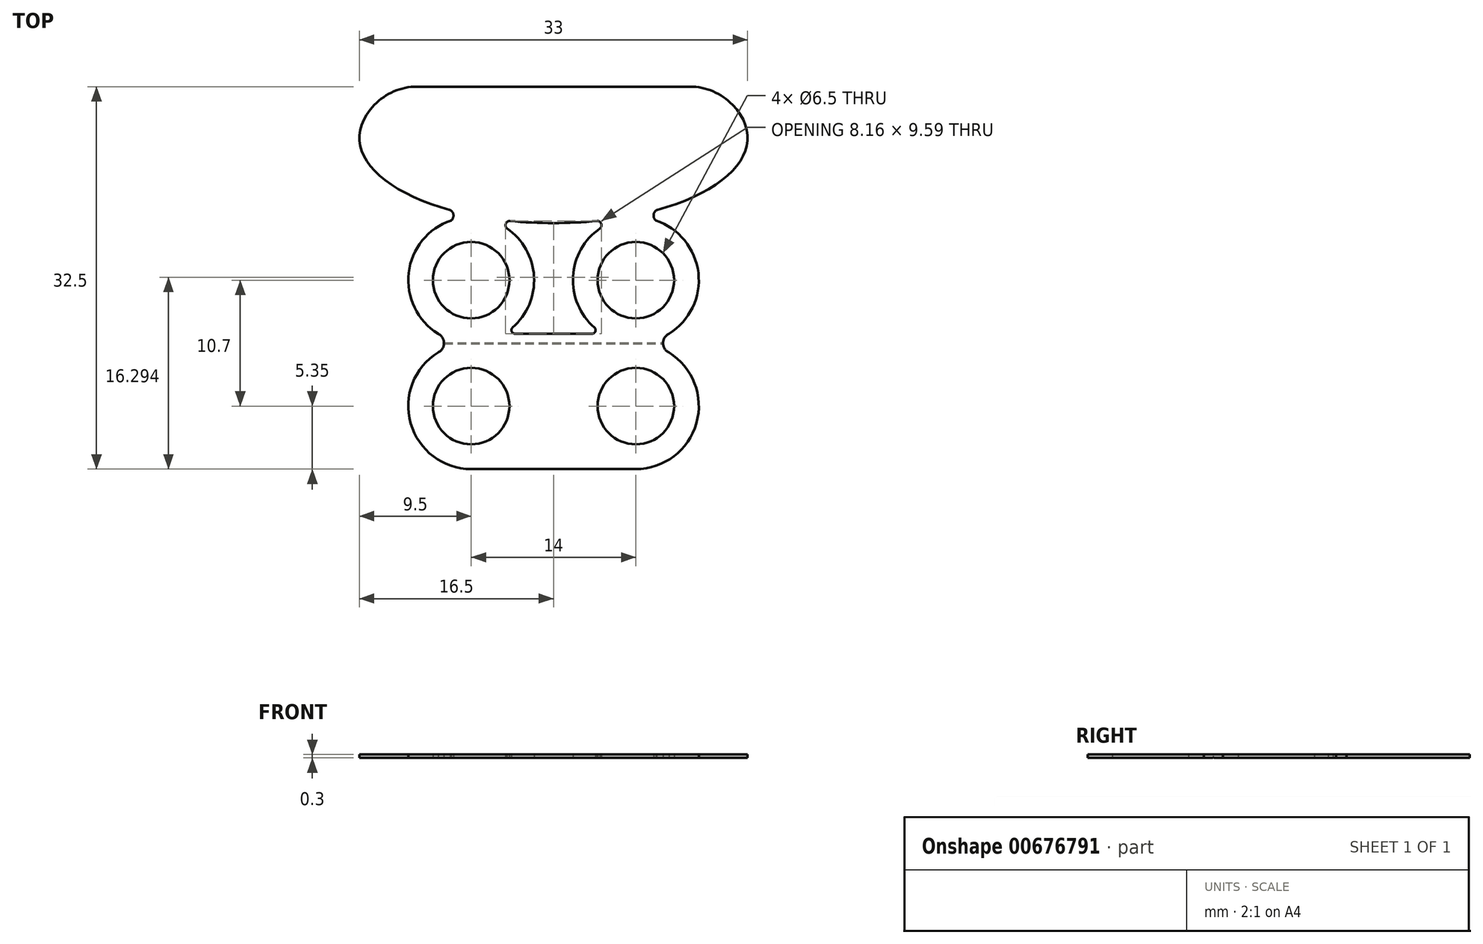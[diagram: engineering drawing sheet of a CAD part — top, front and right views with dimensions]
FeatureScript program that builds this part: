
annotation { "Feature Type Name" : "Feature", "Feature Type Description" : "" }
export const myFeature = defineFeature(function(context is Context, id is Id, definition is map)
    precondition{}
    {
        {
            var Q0;
            Q0=qCreatedBy(makeId("Top.planeOp"),FACE);
            var sketch = newSketch(context, id + "F0", { "sketchPlane" : qUnion([Q0])});
            skLineSegment(sketch, "E0", {"start": v(-13.2, 4.35) * mm, "end": v(13.2, 4.35) * mm});
            skPoint(sketch, "E1", {"position": v(0, -7.25) * mm});
            skCircle(sketch, "E2", {"center": v(-7, -12.1) * mm, "radius": 3.25 * mm});
            skLineSegment(sketch, "E3", {"start": v(0, 24.36) * mm, "end": v(0, -25.37) * mm, "construction": true});
            skPoint(sketch, "E4", {"position": v(-7, -17.45) * mm});
            skEllipticalArc(sketch, "E5", {});
            skEllipticalArc(sketch, "E6", {"construction": true});
            skEllipticalArc(sketch, "E7", {"construction": true});
            skEllipticalArc(sketch, "E8", {});
            skArc(sketch, "E9", {"start": v(-8.7, -7.03) * mm, "mid": v(-12.32, -11.56) * mm, "end": v(-9.68, -16.73) * mm});
            skArc(sketch, "E10", {"start": v(-3.96, -7.7) * mm, "mid": v(-6.25, -6.8) * mm, "end": v(-8.7, -7.03) * mm, "construction": true});
            skCircle(sketch, "E11.MirrorC", {"center": v(7, -12.1) * mm, "radius": 3.25 * mm});
            skArc(sketch, "E12.MirrorCS", {"start": v(8.7, -7.03) * mm, "mid": v(12.32, -11.56) * mm, "end": v(9.68, -16.73) * mm});
            skEllipticalArc(sketch, "E13", {"construction": true});
            skEllipticalArc(sketch, "E14", {});
            skLineSegment(sketch, "E15", {"start": v(-7, -17.45) * mm, "end": v(7, -17.45) * mm, "construction": true});
            skCircle(sketch, "E16.MirrorC", {"center": v(7, -22.8) * mm, "radius": 3.25 * mm});
            skCircle(sketch, "E17.MirrorC", {"center": v(-7, -22.8) * mm, "radius": 3.25 * mm});
            skPoint(sketch, "E18", {"position": v(-7, -28.15) * mm});
            skLineSegment(sketch, "E19", {"start": v(-7, -28.15) * mm, "end": v(7, -28.15) * mm});
            skLineSegment(sketch, "E20", {"start": v(-4.19, -16.65) * mm, "end": v(4.19, -16.65) * mm});
            skArc(sketch, "E21", {"start": v(-9.81, -18.25) * mm, "mid": v(-9.31, -17.45) * mm, "end": v(-9.81, -16.65) * mm});
            skLineSegment(sketch, "E22", {"start": v(-9.81, -16.65) * mm, "end": v(-9.81, -18.25) * mm, "construction": true});
            skArc(sketch, "E23.MirrorCS", {"start": v(9.81, -18.25) * mm, "mid": v(9.31, -17.45) * mm, "end": v(9.81, -16.65) * mm});
            skArc(sketch, "E24", {"start": v(-9.68, -16.73) * mm, "mid": v(-6.92, -17.45) * mm, "end": v(-4.19, -16.65) * mm, "construction": true});
            skArc(sketch, "E25", {"start": v(-4.19, -16.65) * mm, "mid": v(-1.65, -12.23) * mm, "end": v(-3.96, -7.7) * mm});
            skArc(sketch, "E26", {"start": v(-9.81, -18.25) * mm, "mid": v(-12.15, -24.26) * mm, "end": v(-7, -28.15) * mm});
            skArc(sketch, "E27", {"start": v(-7, -28.15) * mm, "mid": v(-1.85, -21.34) * mm, "end": v(-9.81, -18.25) * mm, "construction": true});
            skArc(sketch, "E28", {"start": v(9.68, -18.17) * mm, "mid": v(1.83, -21.41) * mm, "end": v(7, -28.15) * mm, "construction": true});
            skArc(sketch, "E29", {"start": v(7, -28.15) * mm, "mid": v(12.17, -24.19) * mm, "end": v(9.68, -18.17) * mm});
            skArc(sketch, "E30", {"start": v(9.68, -16.73) * mm, "mid": v(6.92, -17.45) * mm, "end": v(4.19, -16.65) * mm, "construction": true});
            skArc(sketch, "E31", {"start": v(4.19, -16.65) * mm, "mid": v(1.65, -12.23) * mm, "end": v(3.96, -7.7) * mm});
            skArc(sketch, "E32", {"start": v(-8.7, -7.03) * mm, "mid": v(-8.5, -6.57) * mm, "end": v(-8.77, -6.14) * mm});
            skArc(sketch, "E33", {"start": v(-3.73, -7.06) * mm, "mid": v(-4.06, -7.3) * mm, "end": v(-3.96, -7.7) * mm});
            skArc(sketch, "E34.MirrorCS", {"start": v(3.73, -7.06) * mm, "mid": v(4.06, -7.3) * mm, "end": v(3.96, -7.7) * mm});
            skArc(sketch, "E35.MirrorCS", {"start": v(8.7, -7.03) * mm, "mid": v(8.5, -6.57) * mm, "end": v(8.77, -6.14) * mm});
            const initialGuessF0  = {"E5": [0, 0, 1, 0, 0.0165, 0.00725, 2.49809154479651, 4.152051585814538], "E6": [0, 0, 1, 0, 0.0165, 0.00725, 0.6435011087932834, 2.49809154479651], "E7": [0, 0, 1, 0, 0.0165, 0.00725, 4.152051585814538, 4.484235995839755], "E8": [0, 0, 1, 0, 0.0165, 0.00725, 4.484235995839755, 4.940541964929625], "E13": [0, 0, 1, 0, 0.0165, 0.00725, 4.940541964929625, 5.272726374954841], "E14": [0, 0, 1, 0, 0.0165, 0.00725, 5.272726374954841, 0.6435011087932834]};
            skSetInitialGuess(sketch, initialGuessF0);
            skSolve(sketch);
        }
        {
            var Q0;
            Q0=makeQuery(id+"F0.imprint","IMPRINT",FACE,{"disambiguationData":[TD([[makeQuery(id+"F0.imprint","IMPRINT",EDGE,{"derivedFrom":sQuery(id+"F0.wireOp",EDGE,"E0")}),-1.0]])]});
            extrude(context, id + "F1", {"entities" : qUnion([Q0]), "depth" : 0.3 * mm, "offsetDistance" : 25 * mm});
        }
        {
            var Q0;
            Q0=makeQuery(id+"F1.opExtrude","SWEPT_EDGE",EDGE,{"disambiguationData":[OSD([sQuery(id+"F0.wireOp",EDGE,"E0"),sQuery(id+"F0.wireOp",EDGE,"E14")])]});
            var Q1;
            Q1=makeQuery(id+"F1.opExtrude","SWEPT_EDGE",EDGE,{"disambiguationData":[OSD([sQuery(id+"F0.wireOp",EDGE,"E0"),sQuery(id+"F0.wireOp",EDGE,"E5")])]});
            fillet(context, id + "F2", {"entities" : qUnion([Q0, Q1]), "radius" : 5 * mm, "tangentPropagation" : true, "allowEdgeOverflow" : false});
        }
        {
            var Q0;
            Q0=makeQuery(id+"F1.opExtrude","SWEPT_EDGE",EDGE,{"disambiguationData":[OSD([sQuery(id+"F0.wireOp",EDGE,"E20"),sQuery(id+"F0.wireOp",EDGE,"E25")])]});
            var Q1;
            Q1=makeQuery(id+"F1.opExtrude","SWEPT_EDGE",EDGE,{"disambiguationData":[OSD([sQuery(id+"F0.wireOp",EDGE,"E20"),sQuery(id+"F0.wireOp",EDGE,"E31")])]});
            fillet(context, id + "F3", {"entities" : qUnion([Q0, Q1]), "radius" : 0.3 * mm, "tangentPropagation" : true, "allowEdgeOverflow" : false});
        }
        {
            var Q0;
            Q0=makeQuery(id+"F1.opExtrude","CAP_FACE",FACE,{"disambiguationData":[OSD([sQuery(id+"F0.wireOp",EDGE,"E0"),sQuery(id+"F0.wireOp",EDGE,"E2"),sQuery(id+"F0.wireOp",EDGE,"CHCftW8w-065h-tQDZ-IhoU-abju6eTLG0Pv"),sQuery(id+"F0.wireOp",EDGE,"KbDhvPpw-rd1N-rmwO-lzf3-fwdg6Sh6NQGA"),sQuery(id+"F0.wireOp",EDGE,"E5"),sQuery(id+"F0.wireOp",EDGE,"E8"),sQuery(id+"F0.wireOp",EDGE,"E9"),sQuery(id+"F0.wireOp",EDGE,"d9a823b4-093e-4013-9511-6d8e921653f30.MirrorCS"),sQuery(id+"F0.wireOp",EDGE,"E11.MirrorC"),sQuery(id+"F0.wireOp",EDGE,"E12.MirrorCS"),sQuery(id+"F0.wireOp",EDGE,"d9a823b4-093e-4013-9511-6d8e921653f33.MirrorCS"),sQuery(id+"F0.wireOp",EDGE,"E14"),sQuery(id+"F0.wireOp",EDGE,"E16.MirrorC"),sQuery(id+"F0.wireOp",EDGE,"E17.MirrorC"),sQuery(id+"F0.wireOp",EDGE,"E19"),sQuery(id+"F0.wireOp",EDGE,"E20"),sQuery(id+"F0.wireOp",EDGE,"E21"),sQuery(id+"F0.wireOp",EDGE,"E23.MirrorCS"),sQuery(id+"F0.wireOp",EDGE,"E25"),sQuery(id+"F0.wireOp",EDGE,"E26"),sQuery(id+"F0.wireOp",EDGE,"E29"),sQuery(id+"F0.wireOp",EDGE,"E31")])],"isStart":true});
            var sketch = newSketch(context, id + "F4", { "sketchPlane" : qUnion([Q0])});
            skLineSegment(sketch, "E36", {"start": v(-9.31, 17.45) * mm, "end": v(9.31, 17.45) * mm, "construction": true});
            skLineSegment(sketch, "E37.bottom", {"start": v(-11, 17.5) * mm, "end": v(11, 17.5) * mm});
            skLineSegment(sketch, "E37.top", {"start": v(-11, 17.4) * mm, "end": v(11, 17.4) * mm});
            skLineSegment(sketch, "E37.left", {"start": v(-11, 17.5) * mm, "end": v(-11, 17.4) * mm});
            skLineSegment(sketch, "E37.right", {"start": v(11, 17.5) * mm, "end": v(11, 17.4) * mm});
            skSolve(sketch);
        }
        {
            var Q0;
            Q0 = qSketchRegion(id + "F4", true);
            extrude(context, id + "F5", {"entities" : qUnion([Q0]), "operationType" : NewBodyOperationType.REMOVE, "oppositeDirection" : true, "depth" : 0.05 * mm, "offsetDistance" : 25 * mm});
        }
    });
